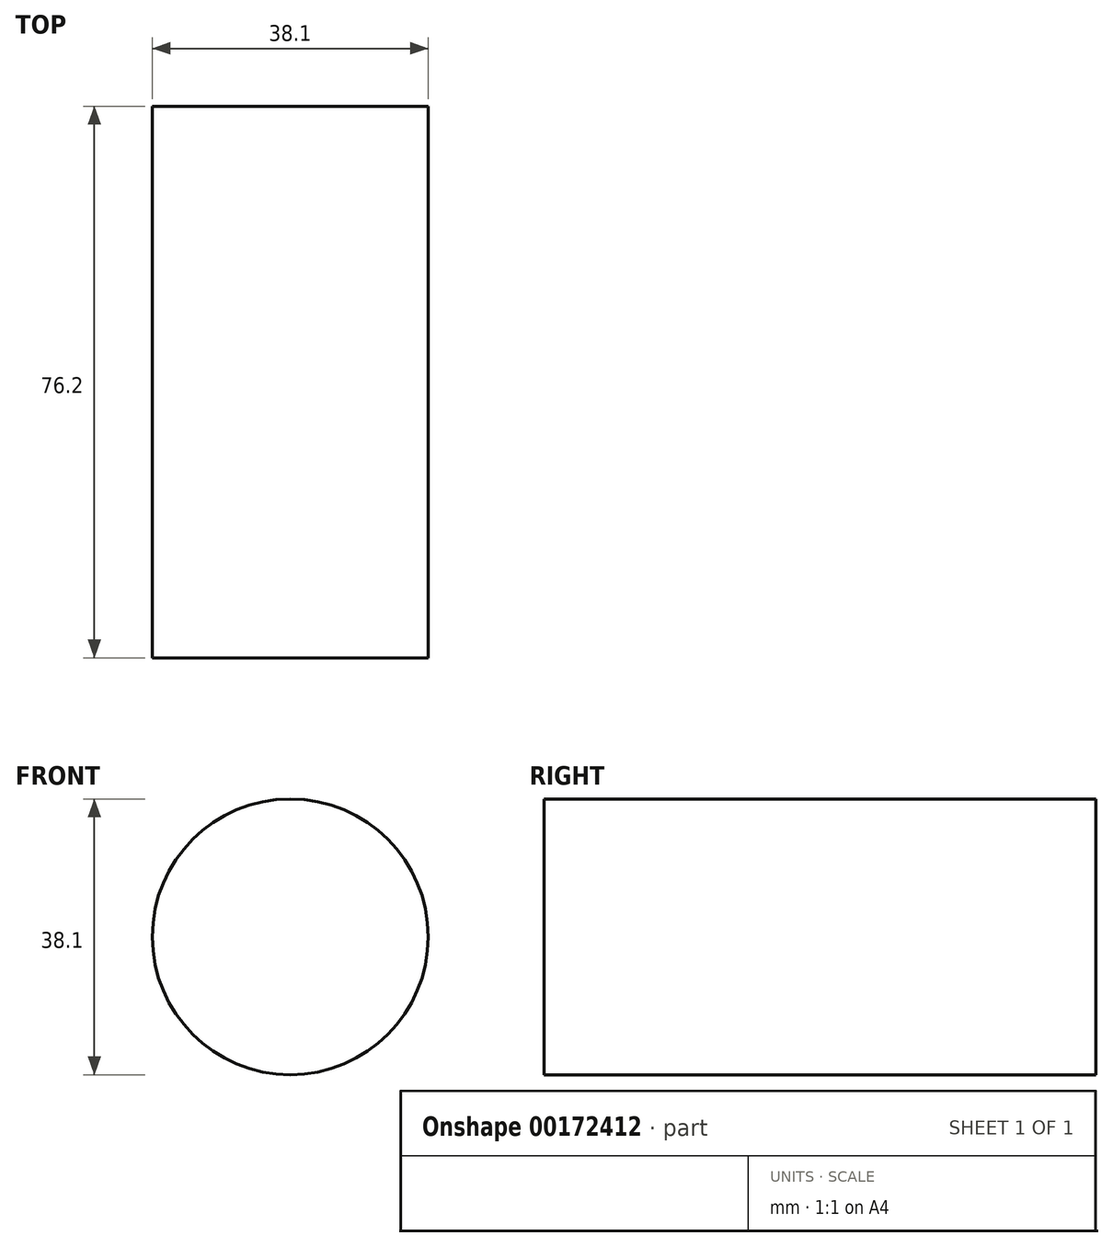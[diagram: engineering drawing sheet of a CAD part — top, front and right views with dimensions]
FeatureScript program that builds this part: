
annotation { "Feature Type Name" : "Feature", "Feature Type Description" : "" }
export const myFeature = defineFeature(function(context is Context, id is Id, definition is map)
    precondition{}
    {
        {
            var Q0;
            Q0=qCreatedBy(makeId("Front.planeOp"),FACE);
            var sketch = newSketch(context, id + "F0", { "sketchPlane" : qUnion([Q0])});
            skCircle(sketch, "E0", {"center": v(0, 0) * mm, "radius": 19.05 * mm});
            skSolve(sketch);
        }
        {
            var Q0;
            Q0 = qSketchRegion(id + "F0", true);
            extrude(context, id + "F1", {"entities" : qUnion([Q0]), "depth" : 76.2 * mm});
        }
    });
